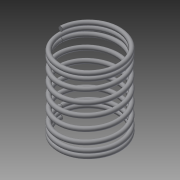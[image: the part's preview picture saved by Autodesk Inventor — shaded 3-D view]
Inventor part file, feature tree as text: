
AUTODESK INVENTOR PART (.ipt)
format: ipt  version: 2014 SP1 (Build 180222100, 222)  size: 358,400 bytes
history: native  units: in
note: dims shown in document units (in); Inventor stores cm internally (conversion verified against a paired STEP export)
features: helix x3, sketch x3, projected_geometry x2, other x1
ambient origin geometry x8: Origin, YZ Plane, XZ Plane, XY Plane, X Axis, Y Axis, Z Axis, Center Point
bodies: Solid1 (feature_tree)
feature tree (9):
  other  "Safety Locking Spring"
  helix  "Coil1"  [1 undecoded]
  helix  "Coil2"  [1 undecoded]
  helix  "Coil3"  [1 undecoded]
  sketch  "Sketch1"  dims[d3=0.1785in]
  sketch  "Sketch2"  dims[d4=0.011in d5=0.1785in]
  projected_geometry  "Projected Loop1"
  sketch  "Sketch3"  dims[d6=0.7874in d7=0.0in d8=90.0deg d9=90.0deg d10=0.0in d11=0.0in d12=0.022in d13=0.022in d14=0.1345in d15=0.011in d16=0.1345in d17=1.9685in d18=0.0in d19=90.0deg d20=90.0deg d21=0.0in d22=0.0in d23=0.011in d24=0.1345in d25=0.7874in d26=0.0in d27=90.0deg d28=90.0deg d29=0.0in d30=0.0in]
  projected_geometry  "Projected Loop2"
note: 3 required parameter values undecoded (feature->parameter linkage not recoverable at this tier; creation-order binding heuristic only, values carry confidence <= 0.55)
